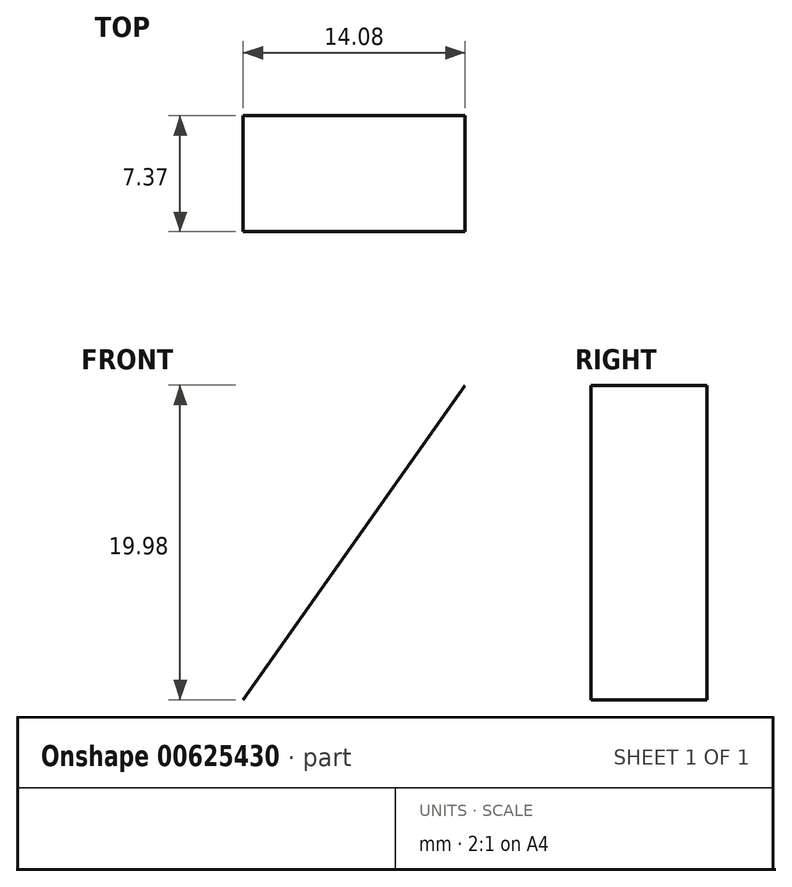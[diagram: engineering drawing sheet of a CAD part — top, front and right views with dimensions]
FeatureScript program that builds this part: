
annotation { "Feature Type Name" : "Feature", "Feature Type Description" : "" }
export const myFeature = defineFeature(function(context is Context, id is Id, definition is map)
    precondition{}
    {
        {
            var Q0;
            Q0=qCreatedBy(makeId("Front.planeOp"),FACE);
            var sketch = newSketch(context, id + "F0", { "sketchPlane" : qUnion([Q0])});
            skCircle(sketch, "E0", {"center": v(0, 0) * mm, "radius": 17.34 * mm});
            skLineSegment(sketch, "E1", {"start": v(0, 17.34) * mm, "end": v(0, 62.84) * mm});
            skLineSegment(sketch, "E2", {"start": v(17.34, 0) * mm, "end": v(70.27, 0) * mm});
            skLineSegment(sketch, "E3", {"start": v(-16.11, -6.42) * mm, "end": v(-78.5, -38.88) * mm});
            skLineSegment(sketch, "E4", {"start": v(122.6, 62.06) * mm, "end": v(136.68, 82.04) * mm});
            skSolve(sketch);
        }
        {
            var Q0;
            Q0=sQuery(id+"F0.wireOp",EDGE,"E4");
            extrude(context, id + "F1", {"bodyType" : ToolBodyType.SURFACE, "surfaceEntities" : qUnion([Q0]), "oppositeDirection" : true, "depth" : 7.37 * mm, "offsetDistance" : 25.4 * mm});
        }
    });
